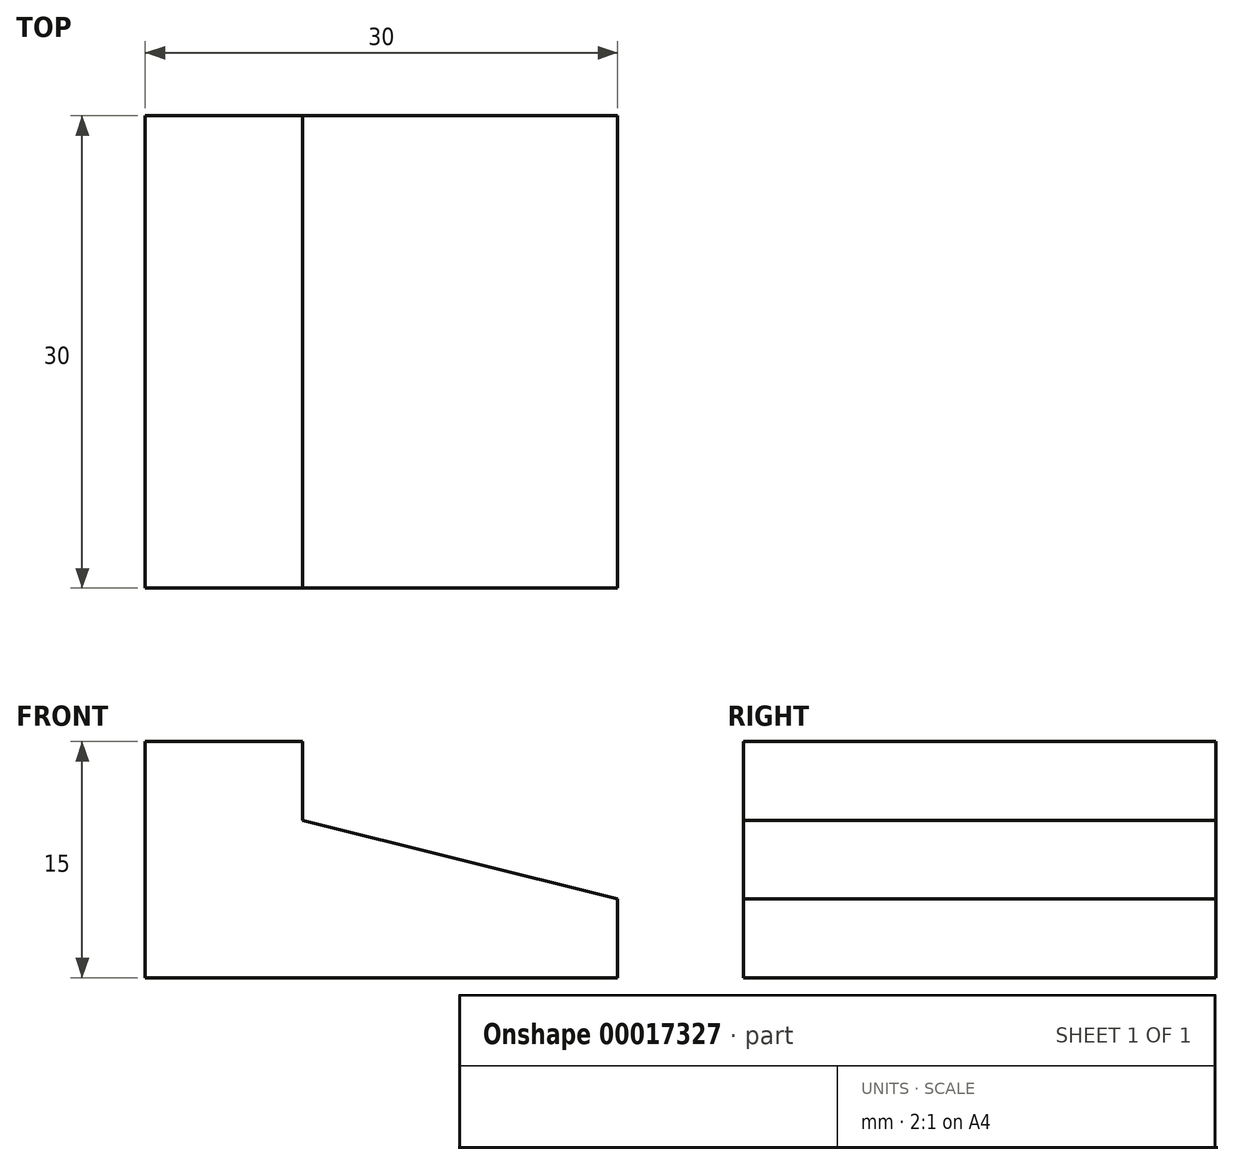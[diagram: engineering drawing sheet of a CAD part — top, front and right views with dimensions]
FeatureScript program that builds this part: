
annotation { "Feature Type Name" : "Feature", "Feature Type Description" : "" }
export const myFeature = defineFeature(function(context is Context, id is Id, definition is map)
    precondition{}
    {
        {
            var Q0;
            Q0=qCreatedBy(makeId("Front.planeOp"),FACE);
            var sketch = newSketch(context, id + "F0", { "sketchPlane" : qUnion([Q0])});
            skLineSegment(sketch, "E0", {"start": v(-28.76, 39.3) * mm, "end": v(-28.76, 24.3) * mm});
            skLineSegment(sketch, "E1", {"start": v(-28.76, 24.3) * mm, "end": v(1.24, 24.3) * mm});
            skLineSegment(sketch, "E2", {"start": v(1.24, 24.3) * mm, "end": v(1.24, 29.3) * mm});
            skLineSegment(sketch, "E3", {"start": v(1.24, 29.3) * mm, "end": v(-18.76, 34.3) * mm});
            skLineSegment(sketch, "E4", {"start": v(-18.76, 34.3) * mm, "end": v(-18.76, 39.3) * mm});
            skLineSegment(sketch, "E5", {"start": v(-18.76, 39.3) * mm, "end": v(-28.76, 39.3) * mm});
            skSolve(sketch);
        }
        {
            var Q0;
            Q0=makeQuery(id+"F0.imprint","IMPRINT",FACE,{"disambiguationData":[TD([[makeQuery(id+"F0.imprint","IMPRINT",EDGE,{"derivedFrom":sQuery(id+"F0.wireOp",EDGE,"E0")}),1.0]])]});
            extrude(context, id + "F1", {"entities" : qUnion([Q0]), "depth" : 30 * mm});
        }
    });
